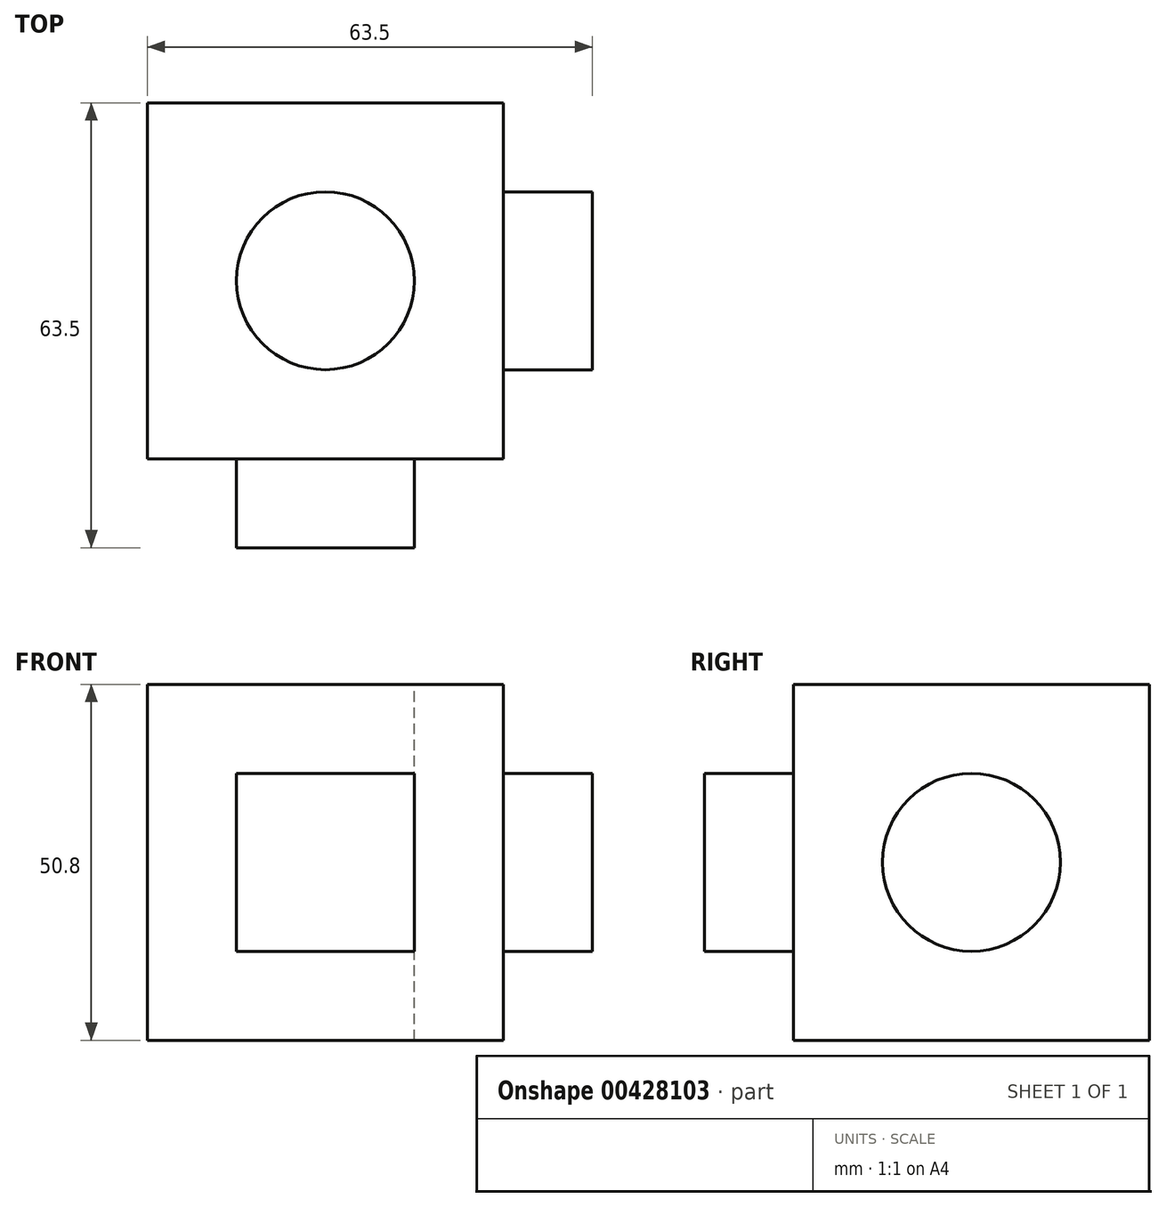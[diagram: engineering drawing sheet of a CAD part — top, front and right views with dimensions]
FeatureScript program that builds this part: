
annotation { "Feature Type Name" : "Feature", "Feature Type Description" : "" }
export const myFeature = defineFeature(function(context is Context, id is Id, definition is map)
    precondition{}
    {
        {
            var Q0;
            Q0=qCreatedBy(makeId("Front.planeOp"),FACE);
            var sketch = newSketch(context, id + "F0", { "sketchPlane" : qUnion([Q0])});
            skLineSegment(sketch, "E0.bottom", {"start": v(0, 0) * mm, "end": v(-50.8, 0) * mm});
            skLineSegment(sketch, "E0.top", {"start": v(0, 50.8) * mm, "end": v(-50.8, 50.8) * mm});
            skLineSegment(sketch, "E0.left", {"start": v(0, 0) * mm, "end": v(0, 50.8) * mm});
            skLineSegment(sketch, "E0.right", {"start": v(-50.8, 0) * mm, "end": v(-50.8, 50.8) * mm});
            skSolve(sketch);
        }
        {
            var Q0;
            Q0 = qSketchRegion(id + "F0", true);
            extrude(context, id + "F1", {"entities" : qUnion([Q0]), "depth" : 50.8 * mm});
        }
        {
            var Q0;
            Q0=makeQuery(id+"F1.opExtrude","CAP_FACE",FACE,{"disambiguationData":[OSD([sQuery(id+"F0.wireOp",EDGE,"E0.bottom"),sQuery(id+"F0.wireOp",EDGE,"E0.top"),sQuery(id+"F0.wireOp",EDGE,"E0.left"),sQuery(id+"F0.wireOp",EDGE,"E0.right")])],"isStart":false});
            var sketch = newSketch(context, id + "F2", { "sketchPlane" : qUnion([Q0])});
            skLineSegment(sketch, "E1.bottom", {"start": v(-38.1, 38.1) * mm, "end": v(-12.7, 38.1) * mm});
            skLineSegment(sketch, "E1.top", {"start": v(-38.1, 12.7) * mm, "end": v(-12.7, 12.7) * mm});
            skLineSegment(sketch, "E1.left", {"start": v(-38.1, 38.1) * mm, "end": v(-38.1, 12.7) * mm});
            skLineSegment(sketch, "E1.right", {"start": v(-12.7, 38.1) * mm, "end": v(-12.7, 12.7) * mm});
            skSolve(sketch);
        }
        {
            var Q0;
            Q0=makeQuery(id+"F2.imprint","IMPRINT",FACE,{"disambiguationData":[TD([[makeQuery(id+"F2.imprint","IMPRINT",EDGE,{"derivedFrom":sQuery(id+"F2.wireOp",EDGE,"E1.bottom")}),-1.0]])]});
            extrude(context, id + "F3", {"entities" : qUnion([Q0]), "operationType" : NewBodyOperationType.ADD, "depth" : 12.7 * mm});
        }
        {
            var Q0;
            Q0=makeQuery(id+"F1.opExtrude","SWEPT_FACE",FACE,{"disambiguationData":[OSD([sQuery(id+"F0.wireOp",EDGE,"E0.left")])]});
            var sketch = newSketch(context, id + "F4", { "sketchPlane" : qUnion([Q0])});
            skCircle(sketch, "E2", {"center": v(-25.4, 25.4) * mm, "radius": 12.7 * mm});
            skPoint(sketch, "E2.centerSnap0", {"position": v(0, 25.4) * mm});
            skPoint(sketch, "E2.centerSnap1", {"position": v(-25.4, 50.8) * mm});
            skSolve(sketch);
        }
        {
            var Q0;
            Q0 = qSketchRegion(id + "F4", true);
            extrude(context, id + "F5", {"entities" : qUnion([Q0]), "operationType" : NewBodyOperationType.ADD, "depth" : 12.7 * mm});
        }
        {
            var Q0;
            Q0=makeQuery(id+"F1.opExtrude","SWEPT_FACE",FACE,{"disambiguationData":[OSD([sQuery(id+"F0.wireOp",EDGE,"E0.top")])]});
            var sketch = newSketch(context, id + "F6", { "sketchPlane" : qUnion([Q0])});
            skCircle(sketch, "E3", {"center": v(-25.4, -25.4) * mm, "radius": 12.7 * mm});
            skPoint(sketch, "E3.centerSnap0", {"position": v(0, -25.4) * mm});
            skPoint(sketch, "E3.centerSnap1", {"position": v(-25.4, 0) * mm});
            skSolve(sketch);
        }
        {
            var Q0;
            Q0 = qSketchRegion(id + "F6", true);
            extrude(context, id + "F7", {"entities" : qUnion([Q0]), "operationType" : NewBodyOperationType.REMOVE, "oppositeDirection" : true, "depth" : 50.8 * mm});
        }
    });
